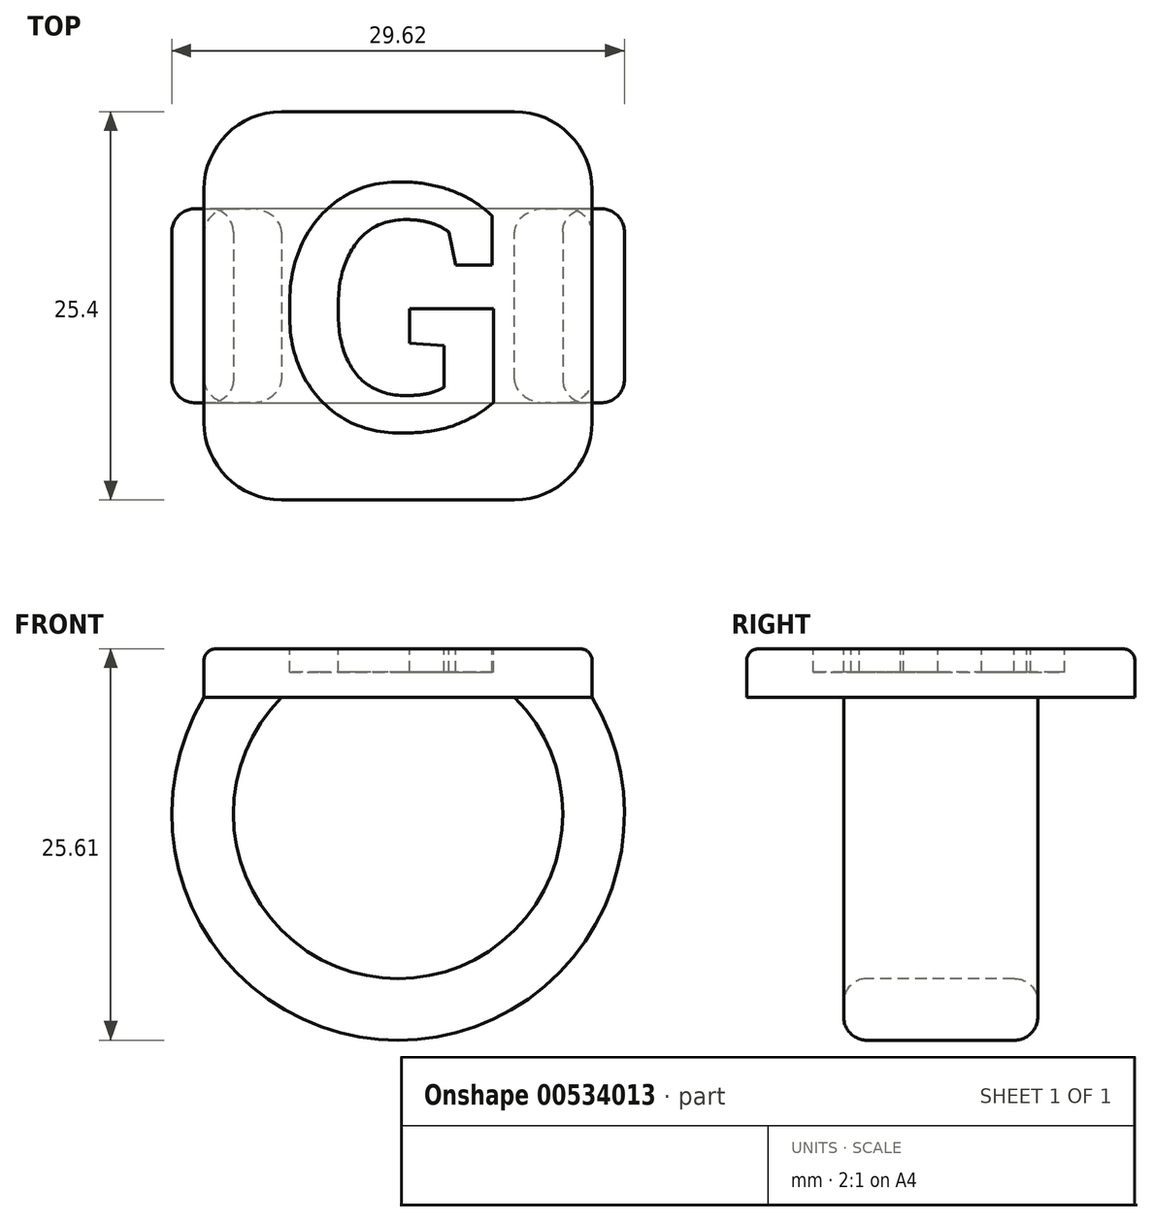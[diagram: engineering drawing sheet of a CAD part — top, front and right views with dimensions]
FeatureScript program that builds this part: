
annotation { "Feature Type Name" : "Feature", "Feature Type Description" : "" }
export const myFeature = defineFeature(function(context is Context, id is Id, definition is map)
    precondition{}
    {
        {
            var Q0;
            Q0=qCreatedBy(makeId("Top.planeOp"),FACE);
            var sketch = newSketch(context, id + "F0", { "sketchPlane" : qUnion([Q0])});
            skLineSegment(sketch, "E0.bottom", {"start": v(12.7, -12.7) * mm, "end": v(-12.7, -12.7) * mm});
            skLineSegment(sketch, "E0.top", {"start": v(12.7, 12.7) * mm, "end": v(-12.7, 12.7) * mm});
            skLineSegment(sketch, "E0.left", {"start": v(12.7, -12.7) * mm, "end": v(12.7, 12.7) * mm});
            skLineSegment(sketch, "E0.right", {"start": v(-12.7, -12.7) * mm, "end": v(-12.7, 12.7) * mm});
            skPoint(sketch, "E0.middle", {"position": v(0, 0) * mm});
            skSolve(sketch);
        }
        {
            var Q0;
            Q0=qSketchRegion(id+"F0",true);
            extrude(context, id + "F1", {"entities" : qUnion([Q0]), "depth" : 3.17 * mm});
        }
        {
            var Q0;
            Q0=qCreatedBy(makeId("Front.planeOp"),FACE);
            var sketch = newSketch(context, id + "F2", { "sketchPlane" : qUnion([Q0])});
            skArc(sketch, "E1", {"start": v(-10.16, 0) * mm, "mid": v(0, -20.32) * mm, "end": v(10.16, 0) * mm});
            skSolve(sketch);
        }
        {
            var Q0;
            Q0=makeQuery(id+"F1.opExtrude","CAP_FACE",FACE,{"disambiguationData":[OSD([sQuery(id+"F0.wireOp",EDGE,"E0.bottom"),sQuery(id+"F0.wireOp",EDGE,"E0.top"),sQuery(id+"F0.wireOp",EDGE,"E0.left"),sQuery(id+"F0.wireOp",EDGE,"E0.right")])],"isStart":true});
            var sketch = newSketch(context, id + "F3", { "sketchPlane" : qUnion([Q0])});
            skLineSegment(sketch, "E2.bottom", {"start": v(-7.62, -6.35) * mm, "end": v(-12.7, -6.35) * mm});
            skLineSegment(sketch, "E2.top", {"start": v(-7.62, 6.35) * mm, "end": v(-12.7, 6.35) * mm});
            skLineSegment(sketch, "E2.left", {"start": v(-7.62, -6.35) * mm, "end": v(-7.62, 6.35) * mm});
            skLineSegment(sketch, "E2.right", {"start": v(-12.7, -6.35) * mm, "end": v(-12.7, 6.35) * mm});
            skPoint(sketch, "E2.middle", {"position": v(-10.16, 0) * mm});
            skSolve(sketch);
        }
        {
            var Q0;
            Q0=qSketchRegion(id+"F3",true);
            var Q1;
            Q1=qConstructionFilter(qBodyType(qCreatedBy(id+"F2",EDGE),BodyType.WIRE),ConstructionObject.NO);
            sweep(context, id + "F4", {"operationType" : NewBodyOperationType.ADD, "profiles" : qUnion([Q0]), "path" : qUnion([Q1])});
        }
        {
            var Q0;
            Q0=qCreatedBy(makeId("Front.planeOp"),FACE);
            var sketch = newSketch(context, id + "F5", { "sketchPlane" : qUnion([Q0])});
            skArc(sketch, "E3.0", {"start": v(9.45, -2.44) * mm, "mid": v(8.62, -1.15) * mm, "end": v(7.62, 0) * mm});
            skLineSegment(sketch, "E3.1", {"start": v(9.45, -2.44) * mm, "end": v(10.16, 0) * mm});
            skLineSegment(sketch, "E3.2", {"start": v(12.7, 0) * mm, "end": v(7.62, 0) * mm});
            skPoint(sketch, "E4.orphan", {"position": v(-7.62, 0) * mm});
            skLineSegment(sketch, "E5.trimOffspring", {"start": v(-7.62, 0) * mm, "end": v(-12.7, 0) * mm});
            skSolve(sketch);
        }
        {
            var Q0;
            Q0=qSketchRegion(id+"F5",true);
            extrude(context, id + "F6", {"entities" : qUnion([Q0]), "operationType" : NewBodyOperationType.ADD, "depth" : 6.35 * mm, "hasSecondDirection" : true, "secondDirectionOppositeDirection" : true, "secondDirectionDepth" : 6.35 * mm});
        }
        {
            var Q0;
            Q0=makeQuery(id+"F1.opExtrude","SWEPT_EDGE",EDGE,{"disambiguationData":[OSD([sQuery(id+"F0.wireOp",EDGE,"E0.bottom"),sQuery(id+"F0.wireOp",EDGE,"E0.left")])]});
            var Q1;
            Q1=makeQuery(id+"F1.opExtrude","SWEPT_EDGE",EDGE,{"disambiguationData":[OSD([sQuery(id+"F0.wireOp",EDGE,"E0.top"),sQuery(id+"F0.wireOp",EDGE,"E0.left")])]});
            var Q2;
            Q2=makeQuery(id+"F1.opExtrude","SWEPT_EDGE",EDGE,{"disambiguationData":[OSD([sQuery(id+"F0.wireOp",EDGE,"E0.top"),sQuery(id+"F0.wireOp",EDGE,"E0.right")])]});
            var Q3;
            Q3=makeQuery(id+"F1.opExtrude","SWEPT_EDGE",EDGE,{"disambiguationData":[OSD([sQuery(id+"F0.wireOp",EDGE,"E0.bottom"),sQuery(id+"F0.wireOp",EDGE,"E0.right")])]});
            fillet(context, id + "F7", {"entities" : qUnion([Q0, Q1, Q2, Q3]), "radius" : 5.08 * mm, "tangentPropagation" : true, "allowEdgeOverflow" : false});
        }
        {
            var Q0;
            Q0=makeQuery(id+"F6.boolean.opBoolean","MERGE",EDGE,{"derivedFrom":[makeQuery(id+"F4.opSweep","SWEPT_EDGE",EDGE,{"disambiguationData":[OSD([sQuery(id+"F2.wireOp",EDGE,"E1"),sQuery(id+"F3.wireOp",EDGE,"E2.top"),sQuery(id+"F3.wireOp",EDGE,"E2.left")])]}),makeQuery(id+"F6.opExtrude","CAP_EDGE",EDGE,{"disambiguationData":[OSD([sQuery(id+"F5.wireOp",EDGE,"E3.0")])],"isStart":false})]});
            var Q1;
            Q1=makeQuery(id+"F4.opSweep","SWEPT_EDGE",EDGE,{"disambiguationData":[OSD([sQuery(id+"F0.wireOp",EDGE,"E0.right"),sQuery(id+"F2.wireOp",EDGE,"E1"),sQuery(id+"F3.wireOp",EDGE,"E2.top"),sQuery(id+"F3.wireOp",EDGE,"E2.right")])]});
            var Q2;
            Q2=makeQuery(id+"F4.opSweep","SWEPT_EDGE",EDGE,{"disambiguationData":[OSD([sQuery(id+"F0.wireOp",EDGE,"E0.right"),sQuery(id+"F2.wireOp",EDGE,"E1"),sQuery(id+"F3.wireOp",EDGE,"E2.bottom"),sQuery(id+"F3.wireOp",EDGE,"E2.right")])]});
            var Q3;
            Q3=makeQuery(id+"F6.boolean.opBoolean","MERGE",EDGE,{"derivedFrom":[makeQuery(id+"F4.opSweep","SWEPT_EDGE",EDGE,{"disambiguationData":[OSD([sQuery(id+"F2.wireOp",EDGE,"E1"),sQuery(id+"F3.wireOp",EDGE,"E2.bottom"),sQuery(id+"F3.wireOp",EDGE,"E2.left")])]}),makeQuery(id+"F6.opExtrude","CAP_EDGE",EDGE,{"disambiguationData":[OSD([sQuery(id+"F5.wireOp",EDGE,"E3.0")])],"isStart":true})]});
            fillet(context, id + "F8", {"entities" : qUnion([Q0, Q1, Q2, Q3]), "radius" : 1.52 * mm, "tangentPropagation" : true, "allowEdgeOverflow" : false});
        }
        {
            var Q0;
            Q0=makeQuery(id+"F1.opExtrude","CAP_EDGE",EDGE,{"disambiguationData":[OSD([sQuery(id+"F0.wireOp",EDGE,"E0.bottom")])],"isStart":false});
            fillet(context, id + "F9", {"entities" : qUnion([Q0]), "radius" : 0.76 * mm, "tangentPropagation" : true, "allowEdgeOverflow" : false});
        }
        {
            var Q0;
            Q0=makeQuery(id+"F1.opExtrude","CAP_FACE",FACE,{"disambiguationData":[OSD([sQuery(id+"F0.wireOp",EDGE,"E0.bottom"),sQuery(id+"F0.wireOp",EDGE,"E0.top"),sQuery(id+"F0.wireOp",EDGE,"E0.left"),sQuery(id+"F0.wireOp",EDGE,"E0.right")])],"isStart":false});
            var sketch = newSketch(context, id + "F10", { "sketchPlane" : qUnion([Q0])});
            skText(sketch, "E6", { "text": "G\n", "fontName": "RobotoSlab-Bold.ttf"});
            skLineSegment(sketch, "E7", {"start": v(-7.62, 0) * mm, "end": v(7.62, 0) * mm, "construction": true});
            skPoint(sketch, "E8", {"position": v(0, 0) * mm});
            const initialGuessF10  = {"E6": [-0.00762, -0.0081, 1, 0, 0.01618]};
            skSetInitialGuess(sketch, initialGuessF10);
            skSolve(sketch);
        }
        {
            var Q0;
            Q0=qSketchRegion(id+"F10",true);
            extrude(context, id + "F11", {"entities" : qUnion([Q0]), "operationType" : NewBodyOperationType.REMOVE, "oppositeDirection" : true, "depth" : 1.52 * mm});
        }
    });
